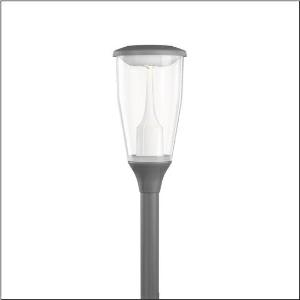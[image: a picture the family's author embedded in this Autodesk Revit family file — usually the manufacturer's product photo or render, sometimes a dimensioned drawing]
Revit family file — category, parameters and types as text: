
# Revit family: dl_11_iq___st1_2a_5xa5575ef14h000022_0b87
name_source: partatom
category: Lighting Fixtures
units: mm (PartAtom-declared; Revit-internal decimal feet)

## family parameters
Cut with Voids When Loaded = No
Host = Face
Light Source = No
Part Type = Normal
Room Calculation Point = No
Round Connector Dimension = Use Diameter
Shared = No

## types (1)
- --- (1 x LED, 1560 lm, 10.5 W, 3000K)
    Apparent Load = 11 VA
    CIE Flux Codes = 24 63 94 96 100
    Color Rendering = 70
    Color Temperature = 3000K
    Default Elevation = 1800 mm
    Description = DL 11 iQ, mast luminaire, Module 540 iQ-SR, primary light control with 3 zone facetted reflector, of plastic, silver coated, highly specular, structured, primary optical cover: cover, of PMMA, transparent, light distribution: ST1.2a, light emission: direct distribution, primary light characteristic: asymmetric, installation type: post-top, LED, High Power LED, rated luminous flux: 1.560lm, luminous efficacy: 149lm/W, light colour: 730, colour temperature: 3000K, control: Street-Remote, Auto-Match, Temp-Guard, Lumen-Switch, Night-Set, Smart-Wire, Light-Fading, Desk-Remote (wireless, voltage-free reading and setting of iQ features in the workshop via application-optimized NFC function/RFID function), optimised constant luminous flux control (CLO 2.0), mains connection: 220..240V, AC, 50/60Hz, connection cable pre-assembled, cable length: 5,5m, start of lifetime: 11W, end of service life: 11W, reduction: 5W, luminaire housing, upper part, of diecast aluminium, coated, Siteco® metallic grey (DB 702S), spigot size: 76mm (post-top), post-top mast mounting element, of diecast aluminium, coated, Siteco® metallic grey (DB 702S), Module 540 iQ-SR, traffic white (RAL 9016), equipment: standard, protection rating (complete): IP66, insulation class (complete): insulation class II (safety insulation), certification: CE, ENEC, ENEC+, VDE, packaging unit: 1 piece

Light Distribution: ST1.2a
    Height = 665 mm
    Lamp = 1 x LED
    Lamp Light Flux = 1560 lm
    Lamp Power = 10.5 W
    Lamp count = 1
    Length = 334 mm
    Luminous efficacy = 149 lm/W
    Manufacturer = Siteco
    ModVariant = No
    Model = 5XA5575EF14H000022
    Number of Poles = 1
    OnlyDefault = Yes
    Power Factor = 1
    Product Name = DL 11 iQ | ST1.2a
    Product group = mast luminaire | pylon top
    ProductGroupID = 6100
    Protection Class = Protection class II
    Protection Degree = IP 66
    RLX_Detail_Level = 1
    RLX_Emergency_Light_Flux = 0 lm
    RLX_Emergency_Type = 0
    RLX_Emergency_Type_DB = No
    RlxData = <blob elided: 152729 chars, md5=2b2f0ab2>
    Socket = socket
    Standby Power = 0 W
    System Light Flux = 1560 lm
    System Power = 11 W
    Type Comments = factory setting: luminous flux: 100 % | dim-lin: 254 | 419 mA
    Type Image = l_1258354.jpg
    URL = http://relux.com
    VarID = @adj_025773
    Voltage = 0 V
    Weight = 0.00 kg
    Width = 0 mm  [stored 0 ft]

note: [stored X ft] marks values corroborated as IEEE doubles in the binary element streams (Revit-internal decimal feet)

## geometry (parser evidence)
native form markers: Blend x4, Sweep x11
no freeform markers — native parametric forms only
